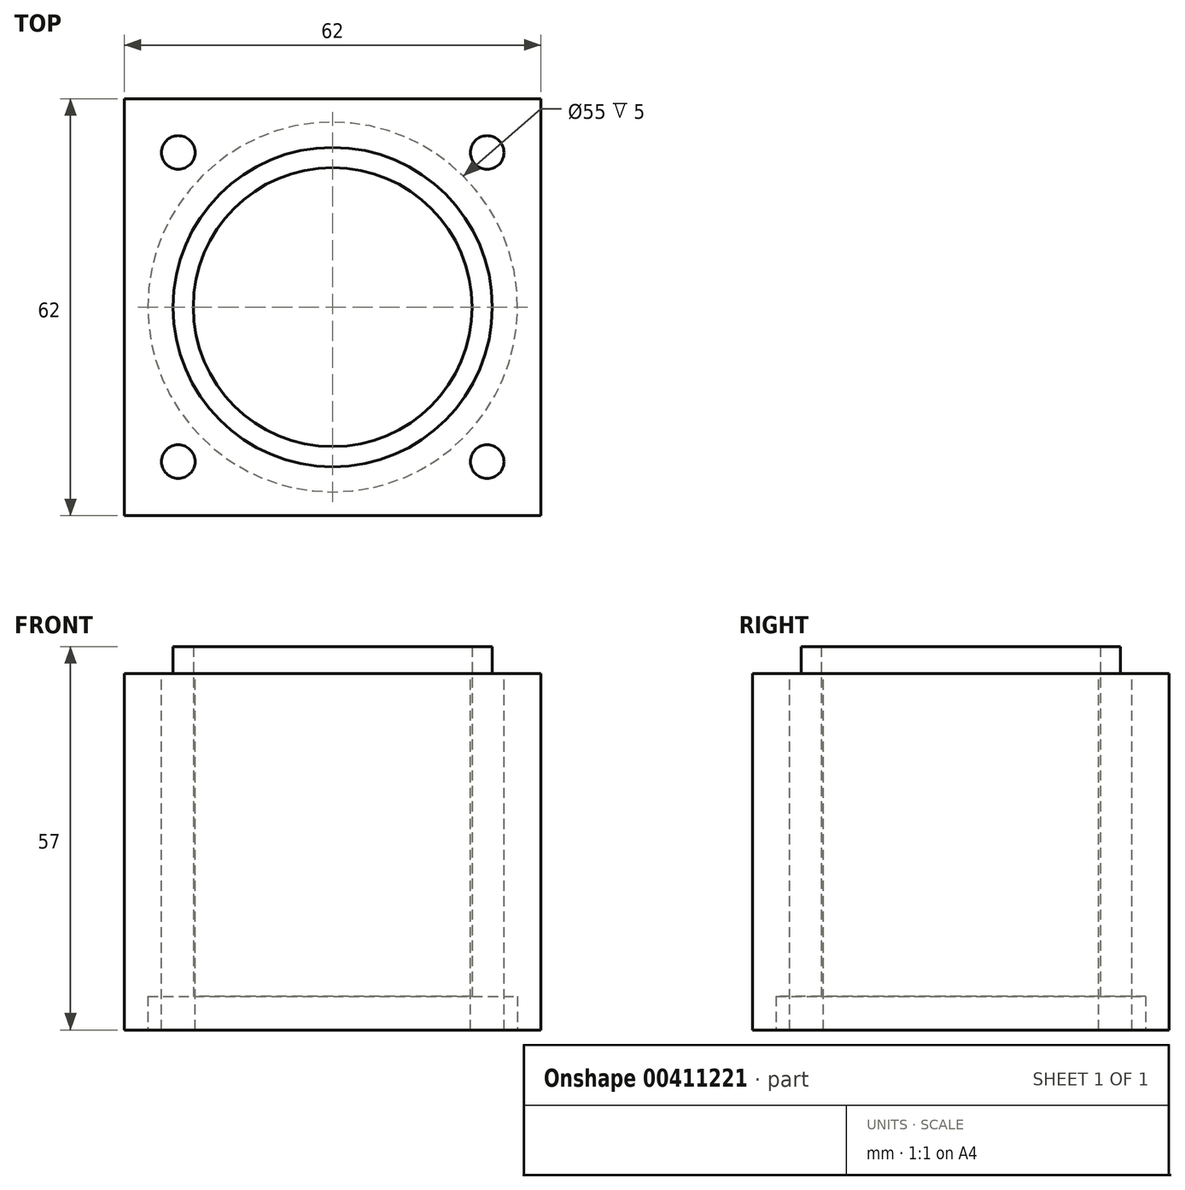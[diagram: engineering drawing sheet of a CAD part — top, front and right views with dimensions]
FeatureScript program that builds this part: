
annotation { "Feature Type Name" : "Feature", "Feature Type Description" : "" }
export const myFeature = defineFeature(function(context is Context, id is Id, definition is map)
    precondition{}
    {
        {
            var Q0;
            Q0=qCreatedBy(makeId("Top.planeOp"),FACE);
            var sketch = newSketch(context, id + "F0", { "sketchPlane" : qUnion([Q0])});
            skLineSegment(sketch, "E0.bottom", {"start": v(31, 31) * mm, "end": v(-31, 31) * mm});
            skLineSegment(sketch, "E0.top", {"start": v(31, -31) * mm, "end": v(-31, -31) * mm});
            skLineSegment(sketch, "E0.left", {"start": v(31, 31) * mm, "end": v(31, -31) * mm});
            skLineSegment(sketch, "E0.right", {"start": v(-31, 31) * mm, "end": v(-31, -31) * mm});
            skPoint(sketch, "E0.middle", {"position": v(0, 0) * mm});
            skCircle(sketch, "E1", {"center": v(0, 0) * mm, "radius": 20.75 * mm});
            skSolve(sketch);
        }
        {
            var Q0;
            Q0 = qSketchRegion(id + "F0", true);
            extrude(context, id + "F1", {"entities" : qUnion([Q0]), "depth" : 53 * mm});
        }
        {
            var Q0;
            Q0=makeQuery(id+"F1.opExtrude","CAP_FACE",FACE,{"disambiguationData":[OSD([sQuery(id+"F0.wireOp",EDGE,"E0.bottom"),sQuery(id+"F0.wireOp",EDGE,"E0.top"),sQuery(id+"F0.wireOp",EDGE,"E0.left"),sQuery(id+"F0.wireOp",EDGE,"E0.right"),sQuery(id+"F0.wireOp",EDGE,"E1")])],"isStart":false});
            var sketch = newSketch(context, id + "F2", { "sketchPlane" : qUnion([Q0])});
            skCircle(sketch, "E2", {"center": v(0, 0) * mm, "radius": 23.75 * mm});
            skCircle(sketch, "E3", {"center": v(0, 0) * mm, "radius": 20.75 * mm});
            skSolve(sketch);
        }
        {
            var Q0;
            Q0 = qSketchRegion(id + "F2", true);
            extrude(context, id + "F3", {"entities" : qUnion([Q0]), "operationType" : NewBodyOperationType.ADD, "depth" : 4 * mm});
        }
        {
            var Q0;
            Q0=makeQuery(id+"F1.opExtrude","CAP_FACE",FACE,{"disambiguationData":[OSD([sQuery(id+"F0.wireOp",EDGE,"E0.bottom"),sQuery(id+"F0.wireOp",EDGE,"E0.top"),sQuery(id+"F0.wireOp",EDGE,"E0.left"),sQuery(id+"F0.wireOp",EDGE,"E0.right"),sQuery(id+"F0.wireOp",EDGE,"E1")])],"isStart":true});
            var sketch = newSketch(context, id + "F4", { "sketchPlane" : qUnion([Q0])});
            skCircle(sketch, "E4", {"center": v(0, 0) * mm, "radius": 27.5 * mm});
            skCircle(sketch, "E5", {"center": v(0, 0) * mm, "radius": 20.75 * mm});
            skSolve(sketch);
        }
        {
            var Q0;
            Q0 = qSketchRegion(id + "F4", true);
            extrude(context, id + "F5", {"entities" : qUnion([Q0]), "operationType" : NewBodyOperationType.REMOVE, "oppositeDirection" : true, "depth" : 5 * mm});
        }
        {
            var Q0;
            Q0=makeQuery(id+"F1.opExtrude","CAP_FACE",FACE,{"disambiguationData":[OSD([sQuery(id+"F0.wireOp",EDGE,"E0.bottom"),sQuery(id+"F0.wireOp",EDGE,"E0.top"),sQuery(id+"F0.wireOp",EDGE,"E0.left"),sQuery(id+"F0.wireOp",EDGE,"E0.right"),sQuery(id+"F0.wireOp",EDGE,"E1")])],"isStart":false});
            var sketch = newSketch(context, id + "F6", { "sketchPlane" : qUnion([Q0])});
            skCircle(sketch, "E6", {"center": v(0, 0) * mm, "radius": 32.5 * mm});
            skLineSegment(sketch, "E7", {"start": v(0, 0) * mm, "end": v(31, 31) * mm});
            skCircle(sketch, "E8", {"center": v(22.98, 22.98) * mm, "radius": 2.5 * mm});
            skCircle(sketch, "E9.1.0", {"center": v(-22.98, 22.98) * mm, "radius": 2.5 * mm});
            skCircle(sketch, "E9.2.0", {"center": v(-22.98, -22.98) * mm, "radius": 2.5 * mm});
            skCircle(sketch, "E9.3.0", {"center": v(22.98, -22.98) * mm, "radius": 2.5 * mm});
            skSolve(sketch);
        }
        {
            var Q0;
            {var subQ0=sQuery(id+"F6.wireOp",EDGE,"E9.1.0");var subQ1=sQuery(id+"F6.wireOp",EDGE,"E6");var subQ2=makeQuery(id+"F6.imprint","INTERSECT",VERTEX,{"disambiguationData":[OD(0.0)],"derivedFrom":[subQ1,subQ0]});Q0=makeQuery(id+"F6.imprint","IMPRINT",FACE,{"disambiguationData":[TD([[makeQuery(id+"F6.imprint","IMPRINT",EDGE,{"disambiguationData":[TD([[subQ2,-1.0]])],"derivedFrom":subQ1}),-1.0]])]});}
            var Q1;
            {var subQ0=sQuery(id+"F6.wireOp",EDGE,"E9.1.0");var subQ1=sQuery(id+"F6.wireOp",EDGE,"E6");var subQ2=makeQuery(id+"F6.imprint","INTERSECT",VERTEX,{"disambiguationData":[OD(0.0)],"derivedFrom":[subQ1,subQ0]});Q1=makeQuery(id+"F6.imprint","IMPRINT",FACE,{"disambiguationData":[TD([[makeQuery(id+"F6.imprint","IMPRINT",EDGE,{"disambiguationData":[TD([[subQ2,-1.0]])],"derivedFrom":subQ1}),1.0]])]});}
            var Q2;
            {var subQ0=sQuery(id+"F6.wireOp",EDGE,"E7");var subQ1=sQuery(id+"F6.wireOp",EDGE,"E6");var subQ2=makeQuery(id+"F6.imprint","INTERSECT",VERTEX,{"derivedFrom":[subQ1,subQ0]});Q2=makeQuery(id+"F6.imprint","IMPRINT",FACE,{"disambiguationData":[TD([[makeQuery(id+"F6.imprint","IMPRINT",EDGE,{"disambiguationData":[TD([[subQ2,-1.0]])],"derivedFrom":subQ1}),-1.0]])]});}
            var Q3;
            {var subQ0=sQuery(id+"F6.wireOp",EDGE,"E8");var subQ1=sQuery(id+"F6.wireOp",EDGE,"E6");var subQ2=makeQuery(id+"F6.imprint","INTERSECT",VERTEX,{"disambiguationData":[OD(0.0)],"derivedFrom":[subQ1,subQ0]});Q3=makeQuery(id+"F6.imprint","IMPRINT",FACE,{"disambiguationData":[TD([[makeQuery(id+"F6.imprint","IMPRINT",EDGE,{"disambiguationData":[TD([[subQ2,-1.0]])],"derivedFrom":subQ1}),-1.0]])]});}
            var Q4;
            {var subQ0=sQuery(id+"F6.wireOp",EDGE,"E8");var subQ1=sQuery(id+"F6.wireOp",EDGE,"E6");var subQ2=makeQuery(id+"F6.imprint","INTERSECT",VERTEX,{"disambiguationData":[OD(0.0)],"derivedFrom":[subQ1,subQ0]});Q4=makeQuery(id+"F6.imprint","IMPRINT",FACE,{"disambiguationData":[TD([[makeQuery(id+"F6.imprint","IMPRINT",EDGE,{"disambiguationData":[TD([[subQ2,-1.0]])],"derivedFrom":subQ1}),1.0]])]});}
            var Q5;
            {var subQ0=sQuery(id+"F6.wireOp",EDGE,"E7");var subQ1=sQuery(id+"F6.wireOp",EDGE,"E6");var subQ2=makeQuery(id+"F6.imprint","INTERSECT",VERTEX,{"derivedFrom":[subQ1,subQ0]});Q5=makeQuery(id+"F6.imprint","IMPRINT",FACE,{"disambiguationData":[TD([[makeQuery(id+"F6.imprint","IMPRINT",EDGE,{"disambiguationData":[TD([[subQ2,-1.0]])],"derivedFrom":subQ1}),1.0]])]});}
            var Q6;
            {var subQ0=sQuery(id+"F6.wireOp",EDGE,"E9.3.0");var subQ1=sQuery(id+"F6.wireOp",EDGE,"E6");var subQ2=makeQuery(id+"F6.imprint","INTERSECT",VERTEX,{"disambiguationData":[OD(0.0)],"derivedFrom":[subQ1,subQ0]});Q6=makeQuery(id+"F6.imprint","IMPRINT",FACE,{"disambiguationData":[TD([[makeQuery(id+"F6.imprint","IMPRINT",EDGE,{"disambiguationData":[TD([[subQ2,-1.0]])],"derivedFrom":subQ1}),1.0]])]});}
            var Q7;
            {var subQ0=sQuery(id+"F6.wireOp",EDGE,"E9.3.0");var subQ1=sQuery(id+"F6.wireOp",EDGE,"E6");var subQ2=makeQuery(id+"F6.imprint","INTERSECT",VERTEX,{"disambiguationData":[OD(0.0)],"derivedFrom":[subQ1,subQ0]});Q7=makeQuery(id+"F6.imprint","IMPRINT",FACE,{"disambiguationData":[TD([[makeQuery(id+"F6.imprint","IMPRINT",EDGE,{"disambiguationData":[TD([[subQ2,-1.0]])],"derivedFrom":subQ1}),-1.0]])]});}
            var Q8;
            {var subQ0=sQuery(id+"F6.wireOp",EDGE,"E9.2.0");var subQ1=sQuery(id+"F6.wireOp",EDGE,"E6");var subQ2=makeQuery(id+"F6.imprint","INTERSECT",VERTEX,{"disambiguationData":[OD(0.0)],"derivedFrom":[subQ1,subQ0]});Q8=makeQuery(id+"F6.imprint","IMPRINT",FACE,{"disambiguationData":[TD([[makeQuery(id+"F6.imprint","IMPRINT",EDGE,{"disambiguationData":[TD([[subQ2,-1.0]])],"derivedFrom":subQ1}),-1.0]])]});}
            var Q9;
            {var subQ0=sQuery(id+"F6.wireOp",EDGE,"E9.2.0");var subQ1=sQuery(id+"F6.wireOp",EDGE,"E6");var subQ2=makeQuery(id+"F6.imprint","INTERSECT",VERTEX,{"disambiguationData":[OD(0.0)],"derivedFrom":[subQ1,subQ0]});Q9=makeQuery(id+"F6.imprint","IMPRINT",FACE,{"disambiguationData":[TD([[makeQuery(id+"F6.imprint","IMPRINT",EDGE,{"disambiguationData":[TD([[subQ2,-1.0]])],"derivedFrom":subQ1}),1.0]])]});}
            extrude(context, id + "F7", {"entities" : qUnion([Q0, Q1, Q2, Q3, Q4, Q5, Q6, Q7, Q8, Q9]), "operationType" : NewBodyOperationType.REMOVE, "endBound" : BoundingType.THROUGH_ALL, "oppositeDirection" : true, "depth" : 25 * mm});
        }
    });
